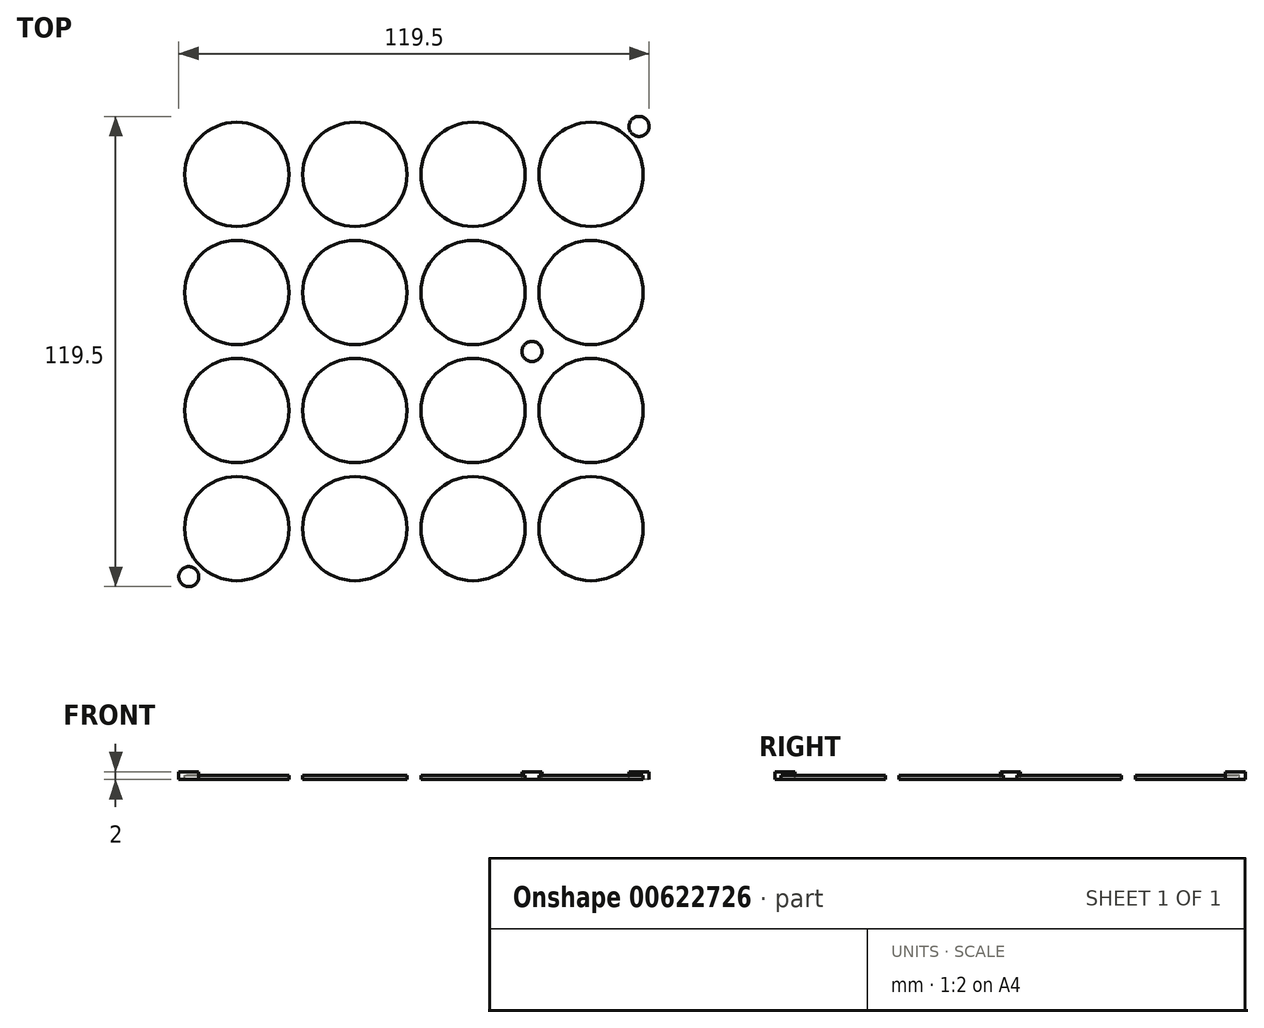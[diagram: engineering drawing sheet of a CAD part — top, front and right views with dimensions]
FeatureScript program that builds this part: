
annotation { "Feature Type Name" : "Feature", "Feature Type Description" : "" }
export const myFeature = defineFeature(function(context is Context, id is Id, definition is map)
    precondition{}
    {
        {
            var Q0;
            Q0=qCreatedBy(makeId("Top.planeOp"),FACE);
            var sketch = newSketch(context, id + "F0", { "sketchPlane" : qUnion([Q0])});
            skLineSegment(sketch, "E0.bottom", {"start": v(-61.25, 61.25) * mm, "end": v(61.25, 61.25) * mm});
            skLineSegment(sketch, "E0.top", {"start": v(-61.25, -61.25) * mm, "end": v(61.25, -61.25) * mm});
            skLineSegment(sketch, "E0.left", {"start": v(-61.25, 61.25) * mm, "end": v(-61.25, -61.25) * mm});
            skLineSegment(sketch, "E0.right", {"start": v(61.25, 61.25) * mm, "end": v(61.25, -61.25) * mm});
            skPoint(sketch, "E0.middle", {"position": v(0, 0) * mm});
            skCircle(sketch, "E1", {"center": v(-45, 45) * mm, "radius": 13.25 * mm});
            skCircle(sketch, "E2.0.1.0", {"center": v(-45, 15) * mm, "radius": 13.25 * mm});
            skCircle(sketch, "E2.0.2.0", {"center": v(-45, -15) * mm, "radius": 13.25 * mm});
            skCircle(sketch, "E2.0.3.0", {"center": v(-45, -45) * mm, "radius": 13.25 * mm});
            skCircle(sketch, "E2.1.0.0", {"center": v(-15, 45) * mm, "radius": 13.25 * mm});
            skCircle(sketch, "E2.1.1.0", {"center": v(-15, 15) * mm, "radius": 13.25 * mm});
            skCircle(sketch, "E2.1.2.0", {"center": v(-15, -15) * mm, "radius": 13.25 * mm});
            skCircle(sketch, "E2.1.3.0", {"center": v(-15, -45) * mm, "radius": 13.25 * mm});
            skCircle(sketch, "E2.2.0.0", {"center": v(15, 45) * mm, "radius": 13.25 * mm});
            skCircle(sketch, "E2.2.1.0", {"center": v(15, 15) * mm, "radius": 13.25 * mm});
            skCircle(sketch, "E2.2.2.0", {"center": v(15, -15) * mm, "radius": 13.25 * mm});
            skCircle(sketch, "E2.2.3.0", {"center": v(15, -45) * mm, "radius": 13.25 * mm});
            skCircle(sketch, "E2.3.0.0", {"center": v(45, 45) * mm, "radius": 13.25 * mm});
            skCircle(sketch, "E2.3.1.0", {"center": v(45, 15) * mm, "radius": 13.25 * mm});
            skCircle(sketch, "E2.3.2.0", {"center": v(45, -15) * mm, "radius": 13.25 * mm});
            skCircle(sketch, "E2.3.3.0", {"center": v(45, -45) * mm, "radius": 13.25 * mm});
            skLineSegment(sketch, "E2.direction1", {"start": v(-45, 45) * mm, "end": v(-15, 45) * mm, "construction": true});
            skLineSegment(sketch, "E2.direction2", {"start": v(-45, 45) * mm, "end": v(-45, 15) * mm, "construction": true});
            skSolve(sketch);
        }
        {
            var Q0;
            Q0=makeQuery(id+"F0.imprint","IMPRINT",FACE,{"disambiguationData":[TD([[makeQuery(id+"F0.imprint","IMPRINT",EDGE,{"derivedFrom":sQuery(id+"F0.wireOp",EDGE,"E1")}),1.0]])]});
            var Q1;
            Q1=makeQuery(id+"F0.imprint","IMPRINT",FACE,{"disambiguationData":[TD([[makeQuery(id+"F0.imprint","IMPRINT",EDGE,{"derivedFrom":sQuery(id+"F0.wireOp",EDGE,"E2.1.0.0")}),1.0]])]});
            var Q2;
            Q2=makeQuery(id+"F0.imprint","IMPRINT",FACE,{"disambiguationData":[TD([[makeQuery(id+"F0.imprint","IMPRINT",EDGE,{"derivedFrom":sQuery(id+"F0.wireOp",EDGE,"E2.2.0.0")}),1.0]])]});
            var Q3;
            Q3=makeQuery(id+"F0.imprint","IMPRINT",FACE,{"disambiguationData":[TD([[makeQuery(id+"F0.imprint","IMPRINT",EDGE,{"derivedFrom":sQuery(id+"F0.wireOp",EDGE,"E2.3.0.0")}),1.0]])]});
            var Q4;
            Q4=makeQuery(id+"F0.imprint","IMPRINT",FACE,{"disambiguationData":[TD([[makeQuery(id+"F0.imprint","IMPRINT",EDGE,{"derivedFrom":sQuery(id+"F0.wireOp",EDGE,"E2.4.0.0")}),1.0]])]});
            var Q5;
            Q5=makeQuery(id+"F0.imprint","IMPRINT",FACE,{"disambiguationData":[TD([[makeQuery(id+"F0.imprint","IMPRINT",EDGE,{"derivedFrom":sQuery(id+"F0.wireOp",EDGE,"E2.4.1.0")}),1.0]])]});
            var Q6;
            Q6=makeQuery(id+"F0.imprint","IMPRINT",FACE,{"disambiguationData":[TD([[makeQuery(id+"F0.imprint","IMPRINT",EDGE,{"derivedFrom":sQuery(id+"F0.wireOp",EDGE,"E2.3.1.0")}),1.0]])]});
            var Q7;
            Q7=makeQuery(id+"F0.imprint","IMPRINT",FACE,{"disambiguationData":[TD([[makeQuery(id+"F0.imprint","IMPRINT",EDGE,{"derivedFrom":sQuery(id+"F0.wireOp",EDGE,"E0.bottom")}),-1.0]])]});
            var Q8;
            Q8=makeQuery(id+"F0.imprint","IMPRINT",FACE,{"disambiguationData":[TD([[makeQuery(id+"F0.imprint","IMPRINT",EDGE,{"derivedFrom":sQuery(id+"F0.wireOp",EDGE,"E2.1.1.0")}),1.0]])]});
            var Q9;
            Q9=makeQuery(id+"F0.imprint","IMPRINT",FACE,{"disambiguationData":[TD([[makeQuery(id+"F0.imprint","IMPRINT",EDGE,{"derivedFrom":sQuery(id+"F0.wireOp",EDGE,"E2.0.1.0")}),1.0]])]});
            var Q10;
            Q10=makeQuery(id+"F0.imprint","IMPRINT",FACE,{"disambiguationData":[TD([[makeQuery(id+"F0.imprint","IMPRINT",EDGE,{"derivedFrom":sQuery(id+"F0.wireOp",EDGE,"E2.2.1.0")}),1.0]])]});
            var Q11;
            Q11=makeQuery(id+"F0.imprint","IMPRINT",FACE,{"disambiguationData":[TD([[makeQuery(id+"F0.imprint","IMPRINT",EDGE,{"derivedFrom":sQuery(id+"F0.wireOp",EDGE,"E2.2.2.0")}),1.0]])]});
            var Q12;
            Q12=makeQuery(id+"F0.imprint","IMPRINT",FACE,{"disambiguationData":[TD([[makeQuery(id+"F0.imprint","IMPRINT",EDGE,{"derivedFrom":sQuery(id+"F0.wireOp",EDGE,"E2.1.2.0")}),1.0]])]});
            var Q13;
            Q13=makeQuery(id+"F0.imprint","IMPRINT",FACE,{"disambiguationData":[TD([[makeQuery(id+"F0.imprint","IMPRINT",EDGE,{"derivedFrom":sQuery(id+"F0.wireOp",EDGE,"E2.0.2.0")}),1.0]])]});
            var Q14;
            Q14=makeQuery(id+"F0.imprint","IMPRINT",FACE,{"disambiguationData":[TD([[makeQuery(id+"F0.imprint","IMPRINT",EDGE,{"derivedFrom":sQuery(id+"F0.wireOp",EDGE,"E2.3.2.0")}),1.0]])]});
            var Q15;
            Q15=makeQuery(id+"F0.imprint","IMPRINT",FACE,{"disambiguationData":[TD([[makeQuery(id+"F0.imprint","IMPRINT",EDGE,{"derivedFrom":sQuery(id+"F0.wireOp",EDGE,"E2.4.2.0")}),1.0]])]});
            var Q16;
            Q16=makeQuery(id+"F0.imprint","IMPRINT",FACE,{"disambiguationData":[TD([[makeQuery(id+"F0.imprint","IMPRINT",EDGE,{"derivedFrom":sQuery(id+"F0.wireOp",EDGE,"E2.3.3.0")}),1.0]])]});
            var Q17;
            Q17=makeQuery(id+"F0.imprint","IMPRINT",FACE,{"disambiguationData":[TD([[makeQuery(id+"F0.imprint","IMPRINT",EDGE,{"derivedFrom":sQuery(id+"F0.wireOp",EDGE,"E2.4.3.0")}),1.0]])]});
            var Q18;
            Q18=makeQuery(id+"F0.imprint","IMPRINT",FACE,{"disambiguationData":[TD([[makeQuery(id+"F0.imprint","IMPRINT",EDGE,{"derivedFrom":sQuery(id+"F0.wireOp",EDGE,"E2.4.4.0")}),1.0]])]});
            var Q19;
            Q19=makeQuery(id+"F0.imprint","IMPRINT",FACE,{"disambiguationData":[TD([[makeQuery(id+"F0.imprint","IMPRINT",EDGE,{"derivedFrom":sQuery(id+"F0.wireOp",EDGE,"E2.3.4.0")}),1.0]])]});
            var Q20;
            Q20=makeQuery(id+"F0.imprint","IMPRINT",FACE,{"disambiguationData":[TD([[makeQuery(id+"F0.imprint","IMPRINT",EDGE,{"derivedFrom":sQuery(id+"F0.wireOp",EDGE,"E2.2.4.0")}),1.0]])]});
            var Q21;
            Q21=makeQuery(id+"F0.imprint","IMPRINT",FACE,{"disambiguationData":[TD([[makeQuery(id+"F0.imprint","IMPRINT",EDGE,{"derivedFrom":sQuery(id+"F0.wireOp",EDGE,"E2.2.3.0")}),1.0]])]});
            var Q22;
            Q22=makeQuery(id+"F0.imprint","IMPRINT",FACE,{"disambiguationData":[TD([[makeQuery(id+"F0.imprint","IMPRINT",EDGE,{"derivedFrom":sQuery(id+"F0.wireOp",EDGE,"E2.1.4.0")}),1.0]])]});
            var Q23;
            Q23=makeQuery(id+"F0.imprint","IMPRINT",FACE,{"disambiguationData":[TD([[makeQuery(id+"F0.imprint","IMPRINT",EDGE,{"derivedFrom":sQuery(id+"F0.wireOp",EDGE,"E2.1.3.0")}),1.0]])]});
            var Q24;
            Q24=makeQuery(id+"F0.imprint","IMPRINT",FACE,{"disambiguationData":[TD([[makeQuery(id+"F0.imprint","IMPRINT",EDGE,{"derivedFrom":sQuery(id+"F0.wireOp",EDGE,"E2.0.3.0")}),1.0]])]});
            var Q25;
            Q25=makeQuery(id+"F0.imprint","IMPRINT",FACE,{"disambiguationData":[TD([[makeQuery(id+"F0.imprint","IMPRINT",EDGE,{"derivedFrom":sQuery(id+"F0.wireOp",EDGE,"E2.0.4.0")}),1.0]])]});
            extrude(context, id + "F1", {"entities" : qUnion([Q0, Q1, Q2, Q3, Q4, Q5, Q6, Q7, Q8, Q9, Q10, Q11, Q12, Q13, Q14, Q15, Q16, Q17, Q18, Q19, Q20, Q21, Q22, Q23, Q24, Q25]), "depth" : 1 * mm, "offsetDistance" : 25 * mm});
        }
        {
            var Q0;
            Q0=qSketchRegion(id+"F0",true);
            extrude(context, id + "F2", {"entities" : qUnion([Q0]), "operationType" : NewBodyOperationType.ADD, "depth" : 2 * mm, "offsetDistance" : 25 * mm});
        }
        {
            var Q0;
            Q0=makeQuery(id+"F2.opExtrude","CAP_FACE",FACE,{"disambiguationData":[OSD([sQuery(id+"F0.wireOp",EDGE,"E0.bottom"),sQuery(id+"F0.wireOp",EDGE,"E0.top"),sQuery(id+"F0.wireOp",EDGE,"E0.left"),sQuery(id+"F0.wireOp",EDGE,"E0.right"),sQuery(id+"F0.wireOp",EDGE,"E1"),sQuery(id+"F0.wireOp",EDGE,"E2.0.1.0"),sQuery(id+"F0.wireOp",EDGE,"E2.0.2.0"),sQuery(id+"F0.wireOp",EDGE,"E2.0.3.0"),sQuery(id+"F0.wireOp",EDGE,"E2.0.4.0"),sQuery(id+"F0.wireOp",EDGE,"E2.1.0.0"),sQuery(id+"F0.wireOp",EDGE,"E2.1.1.0"),sQuery(id+"F0.wireOp",EDGE,"E2.1.2.0"),sQuery(id+"F0.wireOp",EDGE,"E2.1.3.0"),sQuery(id+"F0.wireOp",EDGE,"E2.1.4.0"),sQuery(id+"F0.wireOp",EDGE,"E2.2.0.0"),sQuery(id+"F0.wireOp",EDGE,"E2.2.1.0"),sQuery(id+"F0.wireOp",EDGE,"E2.2.2.0"),sQuery(id+"F0.wireOp",EDGE,"E2.2.3.0"),sQuery(id+"F0.wireOp",EDGE,"E2.2.4.0"),sQuery(id+"F0.wireOp",EDGE,"E2.3.0.0"),sQuery(id+"F0.wireOp",EDGE,"E2.3.1.0"),sQuery(id+"F0.wireOp",EDGE,"E2.3.2.0"),sQuery(id+"F0.wireOp",EDGE,"E2.3.3.0"),sQuery(id+"F0.wireOp",EDGE,"E2.3.4.0"),sQuery(id+"F0.wireOp",EDGE,"E2.4.0.0"),sQuery(id+"F0.wireOp",EDGE,"E2.4.1.0"),sQuery(id+"F0.wireOp",EDGE,"E2.4.2.0"),sQuery(id+"F0.wireOp",EDGE,"E2.4.3.0"),sQuery(id+"F0.wireOp",EDGE,"E2.4.4.0")])],"isStart":false});
            var sketch = newSketch(context, id + "F3", { "sketchPlane" : qUnion([Q0])});
            skLineSegment(sketch, "E3", {"start": v(0, 74.2) * mm, "end": v(0, -73.43) * mm, "construction": true});
            skLineSegment(sketch, "E4", {"start": v(-81.9, 0) * mm, "end": v(78.5, 0) * mm, "construction": true});
            skCircle(sketch, "E5", {"center": v(-57.2, 57.2) * mm, "radius": 2.55 * mm});
            skCircle(sketch, "E6", {"center": v(-30, 0) * mm, "radius": 2.55 * mm});
            skCircle(sketch, "E7.MirrorC", {"center": v(57.2, 57.2) * mm, "radius": 2.55 * mm});
            skCircle(sketch, "E8.MirrorC", {"center": v(30, 0) * mm, "radius": 2.55 * mm});
            skCircle(sketch, "E9.MirrorC", {"center": v(57.2, -57.2) * mm, "radius": 2.55 * mm});
            skCircle(sketch, "E10.MirrorC", {"center": v(-57.2, -57.2) * mm, "radius": 2.55 * mm});
            skSolve(sketch);
        }
        {
            var Q0;
            Q0=makeQuery(id+"F3.imprint","IMPRINT",FACE,{"disambiguationData":[TD([[makeQuery(id+"F3.imprint","IMPRINT",EDGE,{"derivedFrom":sQuery(id+"F3.wireOp",EDGE,"E5")}),1.0]])]});
            var Q1;
            Q1=makeQuery(id+"F3.imprint","IMPRINT",FACE,{"disambiguationData":[TD([[makeQuery(id+"F3.imprint","IMPRINT",EDGE,{"derivedFrom":sQuery(id+"F3.wireOp",EDGE,"E7.MirrorC")}),-1.0]])]});
            var Q2;
            Q2=makeQuery(id+"F3.imprint","IMPRINT",FACE,{"disambiguationData":[TD([[makeQuery(id+"F3.imprint","IMPRINT",EDGE,{"derivedFrom":sQuery(id+"F3.wireOp",EDGE,"E8.MirrorC")}),-1.0]])]});
            var Q3;
            Q3=makeQuery(id+"F3.imprint","IMPRINT",FACE,{"disambiguationData":[TD([[makeQuery(id+"F3.imprint","IMPRINT",EDGE,{"derivedFrom":sQuery(id+"F3.wireOp",EDGE,"E6")}),1.0]])]});
            var Q4;
            Q4=makeQuery(id+"F3.imprint","IMPRINT",FACE,{"disambiguationData":[TD([[makeQuery(id+"F3.imprint","IMPRINT",EDGE,{"derivedFrom":sQuery(id+"F3.wireOp",EDGE,"E8.MirrorC")}),1.0]])]});
            var Q5;
            Q5=makeQuery(id+"F3.imprint","IMPRINT",FACE,{"disambiguationData":[TD([[makeQuery(id+"F3.imprint","IMPRINT",EDGE,{"derivedFrom":sQuery(id+"F3.wireOp",EDGE,"E6")}),-1.0]])]});
            var Q6;
            Q6=makeQuery(id+"F3.imprint","IMPRINT",FACE,{"disambiguationData":[TD([[makeQuery(id+"F3.imprint","IMPRINT",EDGE,{"derivedFrom":sQuery(id+"F3.wireOp",EDGE,"E10.MirrorC")}),-1.0]])]});
            var Q7;
            Q7=makeQuery(id+"F3.imprint","IMPRINT",FACE,{"disambiguationData":[TD([[makeQuery(id+"F3.imprint","IMPRINT",EDGE,{"derivedFrom":sQuery(id+"F3.wireOp",EDGE,"E9.MirrorC")}),1.0]])]});
            extrude(context, id + "F4", {"entities" : qUnion([Q0, Q1, Q2, Q3, Q4, Q5, Q6, Q7]), "operationType" : NewBodyOperationType.REMOVE, "endBound" : BoundingType.THROUGH_ALL, "oppositeDirection" : true, "depth" : 25 * mm, "offsetDistance" : 25 * mm});
        }
    });
